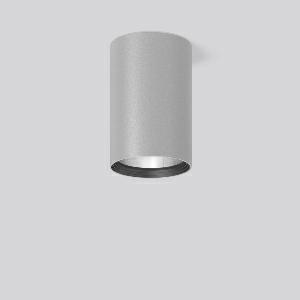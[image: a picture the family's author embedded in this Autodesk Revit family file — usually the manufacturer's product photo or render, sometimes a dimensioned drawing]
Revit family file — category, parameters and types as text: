
# Revit family: heledon_maxi_a_931217_004_1_76_fbff
name_source: partatom
category: Lighting Fixtures
units: mm (PartAtom-declared; Revit-internal decimal feet)

## family parameters
Cut with Voids When Loaded = No
Host = Face
Light Source = No
Part Type = Normal
Room Calculation Point = No
Round Connector Dimension = Use Diameter
Shared = No

## types (1)
- HELEDON maxi A (1 x LED Modul 940, 3500 lm, 4000)
    Apparent Load = 25 VA
    Approval mark = CE
    CIE Flux Codes = 100 100 100 100 100
    Color Rendering = 92
    Color Temperature = 4000
    Default Elevation = 1800 mm
    Description = Series: HELEDON maxi
Cylindrical surface-mounted downlight. Housing: die-cast aluminium, powder-coated. Internal ceiling frame polycarbonate with bayonet mounting. Black plastic ring and recessed LED to prevent glare from the side. Optical assembly with reflector made of MIRO-Silver with 98% total light reflection for outstanding efficiency - can be changed without tools. Best colour rendering index Ra>90. Suitable for Ceiling mounting. Easy installation with a separate ceiling frame with bayonet mounting and plug connection. Driver integrated. Connected via plug-in connector. High quality converter without flickering and stroboscopic effect. The following accessories can be mounted without use of tools: interchangeable lenses, decorative glasses, honeycomb louvre, clear and frosted diffusers, white interchangeable plastic ring. 
Colour: silver
Diameter: 123 mm
Height: 183 mm
Lamp: LED
Socket: without socket
Colour temperature: 4000K
Colour rendering index (CRI): 92
System power: 25 W
Rated luminous flux: 3500 lm
Luminous efficiency: 140 lm/W
Control gear: Converter, dimmable, DALI
Protection class: I
Type of protection: IP 20
    Height = 183 mm
    Lamp = 1 x LED Modul 940
    Lamp Light Flux = 3500 lm
    Lamp count = 1
    Length = 123 mm
    Lifetime = 50000 h
    Luminous efficacy = 140 lm/W
    Manufacturer = RZB
    ModVariant = No
    Model = 931217.004.1.76
    Mounting Place = Ceiling
    Mounting Type = Surface mounted
    Number of Poles = 1
    OnlyDefault = Yes
    Power Factor = 1
    Product Name = HELEDON maxi A
    Product group = Surface mounted downlights
    ProductGroupID = 302
    Protection Class = Protection class I
    Protection Degree = IP 20
    RLX_Detail_Level = 1
    RLX_Emergency_Light_Flux = 0 lm
    RLX_Emergency_Type = 0
    RLX_Emergency_Type_DB = No
    RlxData = <blob elided: 98901 chars, md5=93e70ff7>
    Socket = socket
    Standby Power = 0 W
    System Light Flux = 3500 lm
    System Power = 25 W
    Type Comments = Product without accessories
    Type Image = 931192.004.jpg
    URL = http://relux.com
    VarID = ---
    Voltage = 230 V
    Voltage Range = 220-240 V
    Weight = 0.00 kg
    Width = 0 mm  [stored 0 ft]

note: [stored X ft] marks values corroborated as IEEE doubles in the binary element streams (Revit-internal decimal feet)

## geometry (parser evidence)
native form markers: Blend x4, Sweep x9
no freeform markers — native parametric forms only
